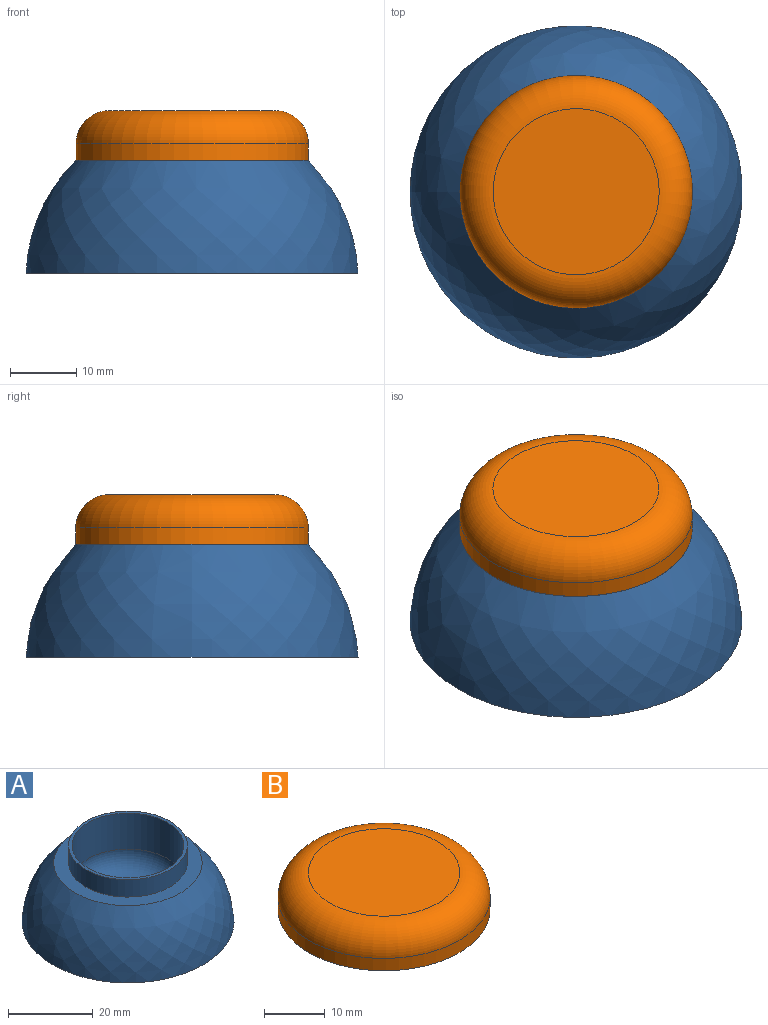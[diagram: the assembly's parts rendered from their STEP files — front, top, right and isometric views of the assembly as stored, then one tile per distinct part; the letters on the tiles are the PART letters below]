
ASSEMBLY  parts=2 mates=1
PART A: 13 faces, bbox 50x50x22 mm
  f0: plane 50x50mm, normal (0,0,-1), area 83.7mm2, adj f1,f12
  f1: revolved ~50x50mm, area 2671.9mm2, adj f0,f2
  f2: plane 35x35mm, normal (0,0,1), area 346.4mm2, adj f1,f3
  f3: cylinder r=14mm len=28mm, axis (0,0,-1), area 439.8mm2, adj f2,f4
  f4: plane 28x28mm, normal (0,0,1), area 69mm2, adj f3,f5
  f5: cylinder r=13.19mm len=26.38mm, axis (0,0,-1), area 860.7mm2, adj f4,f6
  f6: torus R=8.19mm, axis (0,0,-1), area 561.3mm2, adj f5,f7
  f7: plane 16.38x16.38mm, normal (0,0,1), area 210.8mm2, adj f6
  f8: plane 18x18mm, normal (0,0,-1), area 254.5mm2, adj f9
  f9: torus R=9mm, axis (0,0,-1), area 601.2mm2, adj f8,f10
  f10: cone r=14.01mm half-angle=0.1deg, axis (0,0,1), area 470mm2, adj f9,f11
  f11: plane 33.53x33.53mm, normal (0,0,-1), area 266.1mm2, adj f10,f12
  f12: sphere r=24.51mm, area 2516.4mm2, adj f0,f11
PART B: 10 faces, bbox 37.9x37.9x7.5 mm
  f0: cylinder r=14mm len=28mm, axis (0,0,1), area 439.8mm2, adj f1,f9
  f1: plane 29.6x29.6mm, normal (0,0,-1), area 72.4mm2, adj f0,f2
  f2: cylinder r=14.8mm len=29.6mm, axis (0,0,1), area 465mm2, adj f1,f3
  f3: torus R=13.81mm, axis (0,0,1), area 320.9mm2, adj f2,f4
  f4: cylinder r=16.5mm len=33mm, axis (0,0,1), area 259.2mm2, adj f3,f5
  f5: plane 35x35mm, normal (0,0,-1), area 106.8mm2, adj f4,f6
  f6: cylinder r=17.5mm len=35mm, axis (0,0,1), area 274.9mm2, adj f5,f7
  f7: torus R=12.5mm, axis (0,0,1), area 773.9mm2, adj f6,f8
  f8: plane 25x25mm, normal (0,0,1), area 490.9mm2, adj f7
  f9: plane 28x28mm, normal (0,0,-1), area 615.8mm2, adj f0
PLACE A t=(3.11,-4.87,25.6)mm
PLACE B t=(3.11,-4.87,9.11)mm
MATE revolute B.f0 <-> A.f3  axis (0,0,-1) through (3.11,-4.87,40.6)mm
